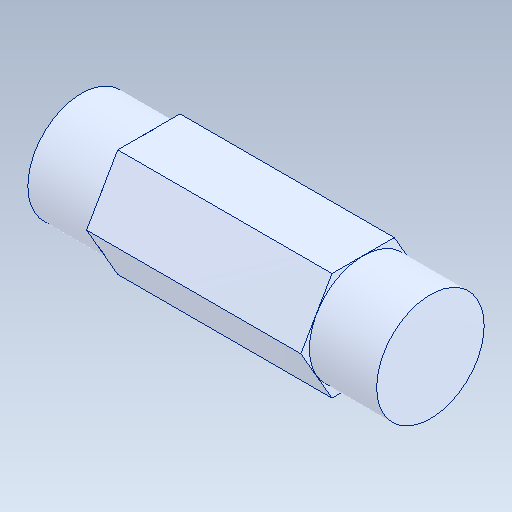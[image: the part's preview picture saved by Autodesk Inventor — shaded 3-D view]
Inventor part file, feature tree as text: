
AUTODESK INVENTOR PART (.ipt)
format: ipt  version: 2020 (Build 240168000, 168)  size: 96,768 bytes
history: native  units: in
note: dims shown in document units (in); Inventor stores cm internally (conversion verified against a paired STEP export)
features: mirror x1
ambient origin geometry x8: Origin, YZ Plane, XZ Plane, XY Plane, X Axis, Y Axis, Z Axis, Center Point
bodies: Solid1 (feature_tree)
feature tree (1):
  mirror  "Mirror1"
